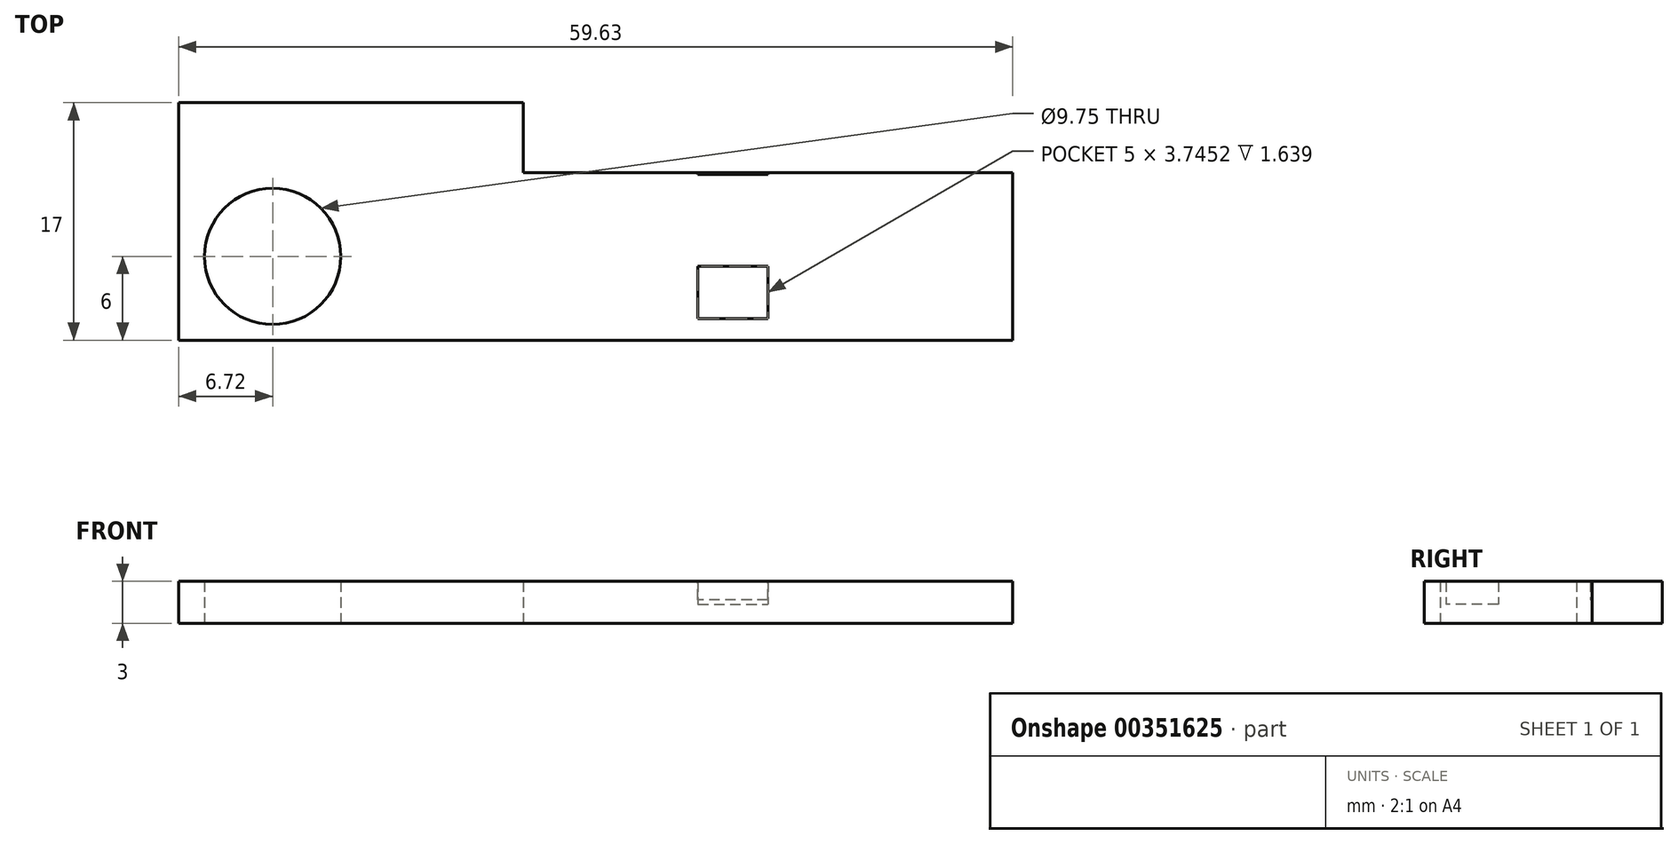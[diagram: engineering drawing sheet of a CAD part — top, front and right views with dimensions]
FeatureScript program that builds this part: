
annotation { "Feature Type Name" : "Feature", "Feature Type Description" : "" }
export const myFeature = defineFeature(function(context is Context, id is Id, definition is map)
    precondition{}
    {
        {
            var Q0;
            Q0=qCreatedBy(makeId("Top.planeOp"),FACE);
            var sketch = newSketch(context, id + "F0", { "sketchPlane" : qUnion([Q0])});
            skLineSegment(sketch, "E0.bottom", {"start": v(17.5, -6) * mm, "end": v(-17.5, -6) * mm});
            skLineSegment(sketch, "E0.top", {"start": v(17.5, 6) * mm, "end": v(-17.5, 6) * mm});
            skLineSegment(sketch, "E0.left", {"start": v(17.5, -6) * mm, "end": v(17.5, 6) * mm});
            skLineSegment(sketch, "E0.right", {"start": v(-17.5, -6) * mm, "end": v(-17.5, 6) * mm});
            skPoint(sketch, "E0.middle", {"position": v(0, 0) * mm});
            skLineSegment(sketch, "E1.bottom", {"start": v(-17.5, -6) * mm, "end": v(-42.13, -6) * mm});
            skLineSegment(sketch, "E1.top", {"start": v(-17.5, 11) * mm, "end": v(-42.13, 11) * mm});
            skLineSegment(sketch, "E1.left", {"start": v(-17.5, -6) * mm, "end": v(-17.5, 11) * mm});
            skLineSegment(sketch, "E1.right", {"start": v(-42.13, -6) * mm, "end": v(-42.13, 11) * mm});
            skCircle(sketch, "E2", {"center": v(-35.4, 0) * mm, "radius": 4.88 * mm});
            skSolve(sketch);
        }
        {
            var Q0;
            {var subQ3=sQuery(id+"F0.wireOp",EDGE,"E1.bottom");Q0=makeQuery(id+"F0.imprint","IMPRINT",FACE,{"disambiguationData":[TD([[makeQuery(id+"F0.imprint","IMPRINT",EDGE,{"derivedFrom":subQ3}),-1.0]])]});}
            var Q1;
            {var subQ0=sQuery(id+"F0.wireOp",EDGE,"E0.bottom");Q1=makeQuery(id+"F0.imprint","IMPRINT",FACE,{"disambiguationData":[TD([[makeQuery(id+"F0.imprint","IMPRINT",EDGE,{"derivedFrom":subQ0}),-1.0]])]});}
            extrude(context, id + "F1", {"entities" : qUnion([Q0, Q1]), "depth" : 3 * mm});
        }
        {
            var Q0;
            Q0=qCreatedBy(makeId("Right.planeOp"),FACE);
            var sketch = newSketch(context, id + "F2", { "sketchPlane" : qUnion([Q0])});
            skLineSegment(sketch, "E3.bottom", {"start": v(9.23, 3.36) * mm, "end": v(5.87, 3.36) * mm});
            skLineSegment(sketch, "E3.top", {"start": v(9.23, 1.68) * mm, "end": v(5.87, 1.68) * mm});
            skLineSegment(sketch, "E3.left", {"start": v(9.23, 3.36) * mm, "end": v(9.23, 1.68) * mm});
            skLineSegment(sketch, "E3.right", {"start": v(5.87, 3.36) * mm, "end": v(5.87, 1.68) * mm});
            skPoint(sketch, "E3.middle", {"position": v(7.55, 2.52) * mm});
            skLineSegment(sketch, "E4.bottom", {"start": v(-0.71, 3.69) * mm, "end": v(-4.46, 3.69) * mm});
            skLineSegment(sketch, "E4.top", {"start": v(-0.71, 1.36) * mm, "end": v(-4.46, 1.36) * mm});
            skLineSegment(sketch, "E4.left", {"start": v(-0.71, 3.69) * mm, "end": v(-0.71, 1.36) * mm});
            skLineSegment(sketch, "E4.right", {"start": v(-4.46, 3.69) * mm, "end": v(-4.46, 1.36) * mm});
            skPoint(sketch, "E4.middle", {"position": v(-2.59, 2.52) * mm});
            skSolve(sketch);
        }
        {
            var Q0;
            Q0=makeQuery(id+"F2.imprint","IMPRINT",FACE,{"disambiguationData":[TD([[makeQuery(id+"F2.imprint","IMPRINT",EDGE,{"derivedFrom":sQuery(id+"F2.wireOp",EDGE,"E3.bottom")}),1.0]])]});
            var Q1;
            Q1=makeQuery(id+"F2.imprint","IMPRINT",FACE,{"disambiguationData":[TD([[makeQuery(id+"F2.imprint","IMPRINT",EDGE,{"derivedFrom":sQuery(id+"F2.wireOp",EDGE,"E4.bottom")}),1.0]])]});
            extrude(context, id + "F3", {"entities" : qUnion([Q0, Q1]), "operationType" : NewBodyOperationType.REMOVE, "oppositeDirection" : true, "depth" : 5 * mm});
        }
    });
